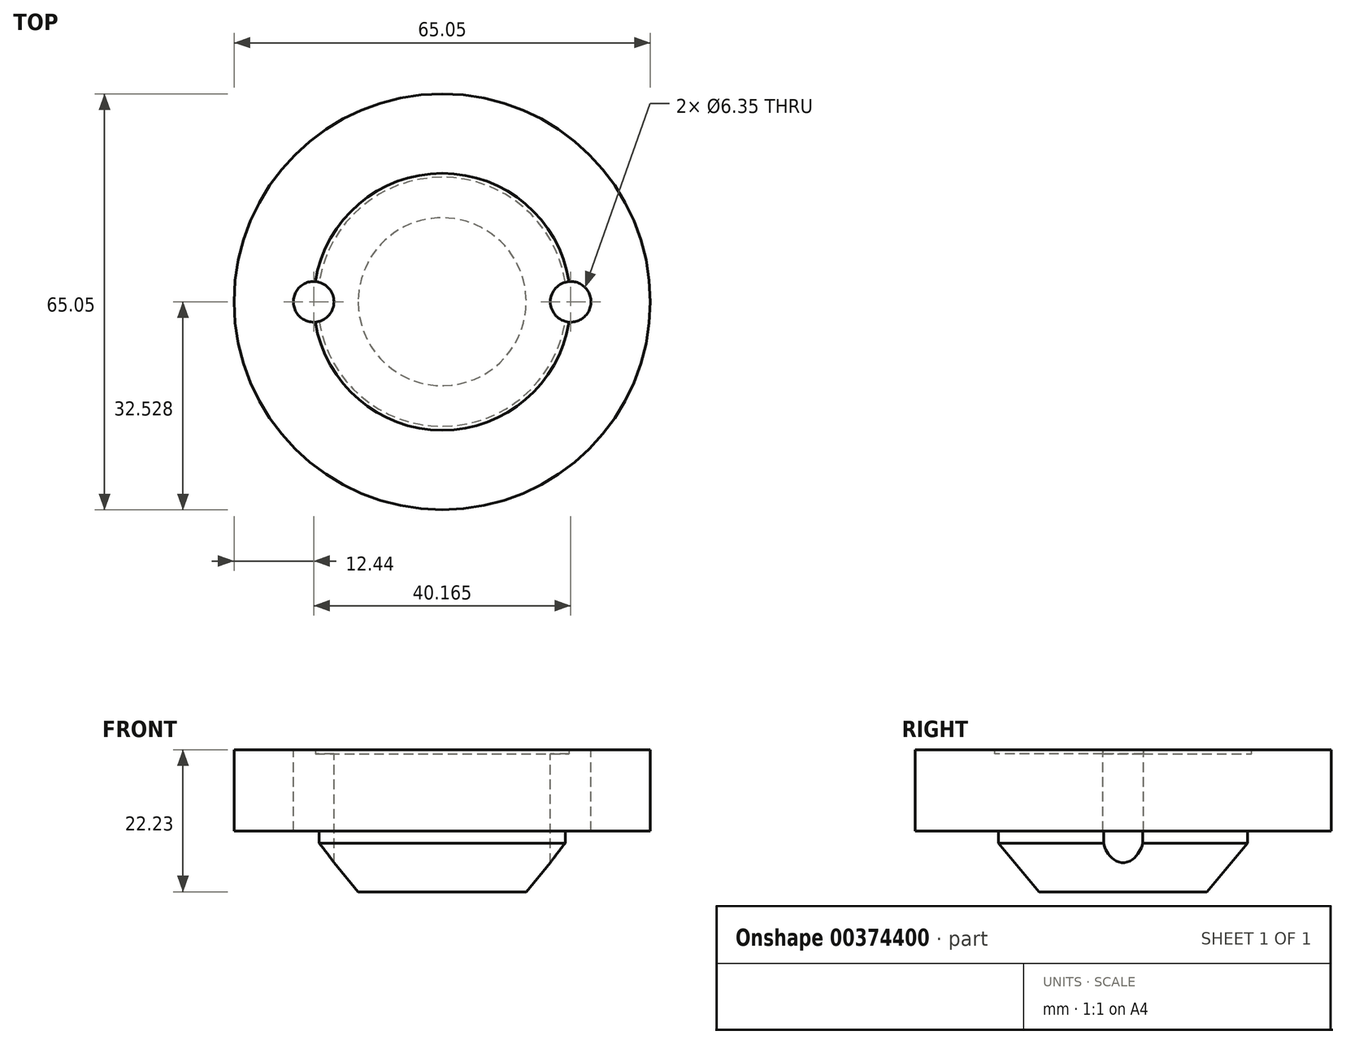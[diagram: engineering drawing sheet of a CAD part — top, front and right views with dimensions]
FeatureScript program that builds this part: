
annotation { "Feature Type Name" : "Feature", "Feature Type Description" : "" }
export const myFeature = defineFeature(function(context is Context, id is Id, definition is map)
    precondition{}
    {
        {
            var Q0;
            Q0=qCreatedBy(makeId("Top.planeOp"),FACE);
            var sketch = newSketch(context, id + "F0", { "sketchPlane" : qUnion([Q0])});
            skCircle(sketch, "E0", {"center": v(-16.12, 12.09) * mm, "radius": 32.52 * mm});
            skSolve(sketch);
        }
        {
            var Q0;
            Q0 = qSketchRegion(id + "F0", true);
            extrude(context, id + "F1", {"entities" : qUnion([Q0]), "depth" : 12.7 * mm});
        }
        {
            var Q0;
            Q0=makeQuery(id+"F1.opExtrude","CAP_FACE",FACE,{"disambiguationData":[OSD([sQuery(id+"F0.wireOp",EDGE,"E0")])],"isStart":true});
            var sketch = newSketch(context, id + "F2", { "sketchPlane" : qUnion([Q0])});
            skCircle(sketch, "E1", {"center": v(-16.12, -12.09) * mm, "radius": 19.48 * mm});
            skSolve(sketch);
        }
        {
            var Q0;
            Q0 = qSketchRegion(id + "F2", true);
            extrude(context, id + "F3", {"entities" : qUnion([Q0]), "operationType" : NewBodyOperationType.ADD, "depth" : 9.52 * mm});
        }
        {
            var Q0;
            Q0=makeQuery(id+"F3.opExtrude","CAP_EDGE",EDGE,{"disambiguationData":[OSD([sQuery(id+"F2.wireOp",EDGE,"E1")])],"isStart":false});
            chamfer(context, id + "F4", {"entities" : qUnion([Q0]), "chamferType" : ChamferType.TWO_OFFSETS, "width1" : 6.35 * mm, "oppositeDirection" : false, "width2" : 7.62 * mm, "tangentPropagation" : true});
        }
        {
            var Q0;
            Q0=makeQuery(id+"F1.opExtrude","CAP_FACE",FACE,{"disambiguationData":[OSD([sQuery(id+"F0.wireOp",EDGE,"E0")])],"isStart":false});
            var sketch = newSketch(context, id + "F5", { "sketchPlane" : qUnion([Q0])});
            skCircle(sketch, "E2", {"center": v(-16.12, 12.09) * mm, "radius": 20.08 * mm});
            skSolve(sketch);
        }
        {
            var Q0;
            Q0 = qSketchRegion(id + "F5", true);
            extrude(context, id + "F6", {"entities" : qUnion([Q0]), "operationType" : NewBodyOperationType.REMOVE, "oppositeDirection" : true, "depth" : 0.64 * mm});
        }
        {
            var Q0;
            Q0=makeQuery(id+"F6.boolean.opBoolean","COPY",FACE,{"derivedFrom":makeQuery(id+"F6.opExtrude","CAP_FACE",FACE,{"disambiguationData":[OSD([sQuery(id+"F5.wireOp",EDGE,"E2")])],"isStart":false})});
            var sketch = newSketch(context, id + "F7", { "sketchPlane" : qUnion([Q0])});
            skLineSegment(sketch, "E3", {"start": v(-16.12, 12.09) * mm, "end": v(-48.34, 12.09) * mm});
            skCircle(sketch, "E4", {"center": v(-36.2, 12.09) * mm, "radius": 3.18 * mm});
            skLineSegment(sketch, "E5", {"start": v(-16.12, 12.09) * mm, "end": v(15.98, 12.09) * mm});
            skCircle(sketch, "E6", {"center": v(3.97, 12.09) * mm, "radius": 3.18 * mm});
            skSolve(sketch);
        }
        {
            var Q0;
            Q0 = qSketchRegion(id + "F7", true);
            extrude(context, id + "F8", {"entities" : qUnion([Q0]), "operationType" : NewBodyOperationType.REMOVE, "endBound" : BoundingType.THROUGH_ALL, "oppositeDirection" : true, "depth" : 25.4 * mm});
        }
        {
            var Q0;
            Q0 = qSketchRegion(id + "F7", true);
            extrude(context, id + "F9", {"entities" : qUnion([Q0]), "operationType" : NewBodyOperationType.REMOVE, "depth" : 19.3 * mm});
        }
    });
